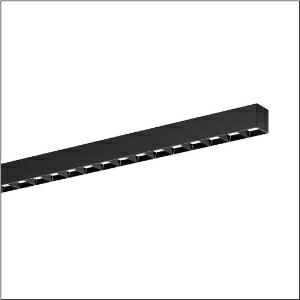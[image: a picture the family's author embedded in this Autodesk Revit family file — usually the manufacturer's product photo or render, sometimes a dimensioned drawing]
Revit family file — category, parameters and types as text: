
# Revit family: silica_r__21_51mx22tctab_4aec
name_source: partatom
category: Lighting Fixtures
units: mm (PartAtom-declared; Revit-internal decimal feet)

## family parameters
Cut with Voids When Loaded = No
Host = Face
Light Source = No
Part Type = Normal
Room Calculation Point = No
Round Connector Dimension = Use Diameter
Shared = No

## types (1)
- --- (1 x LED, 9300 lm, 80.4 W, 6500K)
    Apparent Load = 80 VA
    CIE Flux Codes = 84 100 100 100 100
    Color Rendering = 80
    Color Temperature = 6500K
    Default Elevation = 1800 mm
    Description = Silica® 21, office luminaire, primary light control with darklight reflector, of PMMA, black, CAT 2 (L<= 3000cd/m²), light emission: direct distribution, primary light characteristic: symmetric, installation type: surface-mounted, LED, rated luminous flux: 9.300lm, luminous efficacy: 110lm/W, light colour: 8tw, colour temperature: 2700..6500K, control gear: ECG DALI, with terminal, 3+2-pole, max. 2.5mm², mains connection: 220..240V, AC, 50/60Hz, rated input power: 84.5W, luminaire housing, of aluminium, jet black (RAL 9005), length: 3.004mm, width: 53mm, height: 53mm, protection rating (complete): IP20, insulation class (complete): insulation class I (protective earthing), certification: CE, permissible operating ambient temperature: 0..+35°C, standard: EN 50419, packaging unit: 1 piece
    Height = 0 mm  [stored 0 ft]
    Lamp = 1 x LED
    Lamp Light Flux = 9300 lm
    Lamp Power = 80.4 W
    Lamp count = 1
    Length = 3004 mm
    Luminous efficacy = 116 lm/W
    Manufacturer = Siteco
    ModVariant = No
    Model = 51MX22TCTAB
    Mounting Place = Ceiling
    Mounting Type = Recessed
    Number of Poles = 1
    OnlyDefault = Yes
    Power Factor = 1
    Product Name = Silica® 21
    Product group = office luminaire | ceiling recessed
    ProductGroupID = 400
    Protection Class = Protection class I
    Protection Degree = IP 20
    RLX_Detail_Level = 1
    RLX_Emergency_Light_Flux = 0 lm
    RLX_Emergency_Type = 0
    RLX_Emergency_Type_DB = No
    RlxData = <blob elided: 60585 chars, md5=56110287>
    Socket = socket
    Standby Power = 0 W
    System Light Flux = 9300 lm
    System Power = 80 W
    Type Comments = individual setting
    Type Image = l_1335908.jpg
    URL = http://relux.com
    VarID = @adj_109933
    Voltage = 0 V
    Weight = 0.00 kg
    Width = 53 mm

note: [stored X ft] marks values corroborated as IEEE doubles in the binary element streams (Revit-internal decimal feet)

## geometry (parser evidence)
native form markers: Blend x4, Sweep x13
no freeform markers — native parametric forms only
